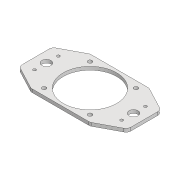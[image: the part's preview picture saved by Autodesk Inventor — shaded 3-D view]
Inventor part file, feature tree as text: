
AUTODESK INVENTOR PART (.ipt)
format: ipt  version: 2020 (Build 240168000, 168)  size: 146,432 bytes
history: native  units: mm
features: mirror x2, other x1, extrude x1
ambient origin geometry x8: Origin, YZ Plane, XZ Plane, XY Plane, X Axis, Y Axis, Z Axis, Center Point
bodies: Body1 (feature_tree)
feature tree (4):
  other  "Sólido1"
  extrude  "Extrusão1"  Depth=65.0mm
  mirror  "Espelhamento1"
  mirror  "Espelhamento3"
